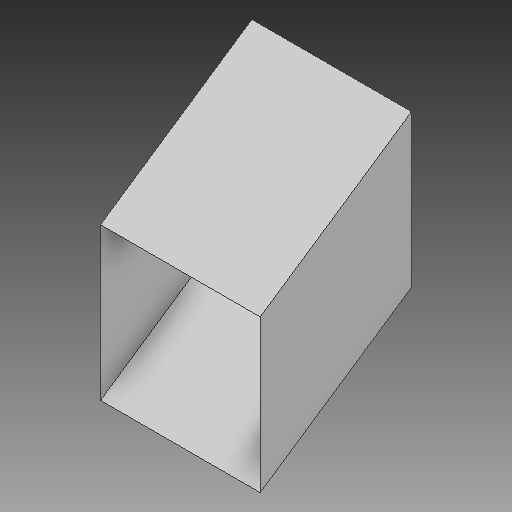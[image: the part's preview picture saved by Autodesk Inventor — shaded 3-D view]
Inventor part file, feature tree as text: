
AUTODESK INVENTOR PART (.ipt)
format: ipt  version: 2017 (Build 210142000, 142)  size: 96,768 bytes
history: native  units: in
note: dims shown in document units (in); Inventor stores cm internally (conversion verified against a paired STEP export)
features: other x2, sketch x2
ambient origin geometry x8: Origin, YZ Plane, XZ Plane, XY Plane, X Axis, Y Axis, Z Axis, Center Point
bodies: Solid1 (feature_tree)
feature tree (4):
  other  "ramp"
  other  "removed ends"
  sketch  "Sketch1"  dims[d0=7.0in]
  sketch  "Sketch2"  dims[d1=6.6667in d2=0.8521in d3=8.0in d4=0.0in d5=0.0in]
